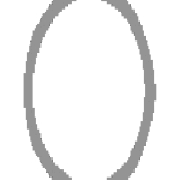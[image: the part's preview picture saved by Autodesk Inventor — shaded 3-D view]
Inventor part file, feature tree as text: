
AUTODESK INVENTOR PART (.ipt)
format: ipt  version: 2021 (Build 250183000, 183)  size: 129,024 bytes
history: native  units: in
note: dims shown in document units (in); Inventor stores cm internally (conversion verified against a paired STEP export)
features: other x4, plane x4, sketch x4, extrude x1, boolean_combine x1
ambient origin geometry x8: Origin, YZ Plane, XZ Plane, XY Plane, X Axis, Y Axis, Z Axis, Center Point
bodies: Solid1 (feature_tree), Body (feature_tree), Solid2 (feature_tree)
feature tree (14):
  other  "Driven Length"
  other  "Frame Generator"
  other  "Start Plane"
  other  "End Plane"
  plane  "Work Plane4"
  plane  "Work Plane5"
  plane  "Work Plane6"
  extrude  "Extrusion3"  Depth=0.065in
  boolean_combine  "Combine1"
  sketch  "Sketch"  dims[d5=12.431in d6=0.12in d7=0.0in d8=90.0deg d9=12.431in d10=0.12in d11=0.0in]
  sketch  "Sketch2"  dims[d0=1.0in d1=0.065in]
  plane  "Work Plane3"
  sketch  "Sketch3"  dims[d2=12.431in]
  sketch  "Sketch4"  dims[d4=-0.0in]
